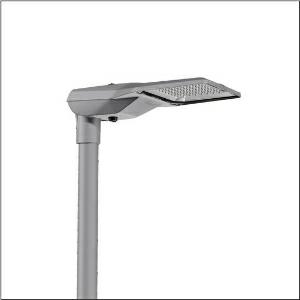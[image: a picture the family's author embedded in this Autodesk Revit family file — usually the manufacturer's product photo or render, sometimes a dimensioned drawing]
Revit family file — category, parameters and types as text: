
# Revit family: streetlight_sl_21_midi___pl52_5xe3h33t08mb_7712
name_source: partatom
category: Lighting Fixtures
units: mm (PartAtom-declared; Revit-internal decimal feet)

## family parameters
Cut with Voids When Loaded = No
Host = Face
Light Source = No
Part Type = Normal
Room Calculation Point = No
Round Connector Dimension = Use Diameter
Shared = No

## types (1)
- --- (1 x LED, 17960 lm, 136 W, 3000K)
    Apparent Load = 136 VA
    CIE Flux Codes = 27 59 98 100 100
    Color Rendering = 70
    Color Temperature = 3000K
    Default Elevation = 1800 mm
    Description = Streetlight SL 21 midi, mast luminaire, primary light control with lens, of PMMA, primary optical cover: cover, of toughened safety glass, transparent, light distribution: PL52, light emission: direct distribution, primary light characteristic: asymmetric, installation type: side-entry, post-top, LED, High Power LED, rated luminous flux: 17.960lm, luminous efficacy: 132lm/W, light colour: 730, colour temperature: 3000K, control gear: D4i, control: overheat protection, constant luminous flux control, time-dependent luminous flux control, flexible luminous flux parameterisation, pre-setting: logarithmic dimming characteristic, mains connection: 230..240V, AC, 50/60Hz, start of lifetime: 136W, end of service life: 142W, reduction: 61W, luminaire housing, of diecast aluminium, powder-coated, SITECO metallic grey (DB 702S), corrosivity category C5 high according to DIN EN ISO 12944, please order mast flange separately, inclination adjustable: 0°, 5°, 10°, 15°, sealing non-destructively replaceable, multi-level sealing system, length: 644mm, width: 335mm, height: 110mm, mast flange for spigot size: 42mm (side-entry): 5XC10008XM4, 60/48mm (side-entry/post-top): 5XC10108XM2, 76/60mm (side-entry/post-top): 5XC10108XM1, mounting height: 4..8m, Smart Interface below and above, protection rating (complete): IP66, insulation class (complete): insulation class II (safety insulation), certification: CE, ENEC, ENEC+, VDE, impact resistance: IK10, permissible operating ambient temperature for outdoor applications: -40..+50°C, standard-compliant lighting for roads and squares, packaging unit: 1 piece

Light Distribution: PL52
    Height = 111 mm
    Lamp = 1 x LED
    Lamp Light Flux = 17960 lm
    Lamp Power = 136 W
    Lamp count = 1
    Length = 644 mm
    Luminous efficacy = 132 lm/W
    Manufacturer = Siteco
    ModVariant = No
    Model = 5XE3H33T08MB
    Number of Poles = 1
    OnlyDefault = Yes
    Power Factor = 1
    Product Name = Streetlight SL 21 midi | PL52
    Product group = mast luminaire | pylon top
    ProductGroupID = 6100
    Protection Class = Protection class II
    Protection Degree = IP 66
    RLX_Detail_Level = 1
    RLX_Emergency_Light_Flux = 0 lm
    RLX_Emergency_Type = 0
    RLX_Emergency_Type_DB = No
    RlxData = <blob elided: 36653 chars, md5=68a0ea8b>
    Socket = socket
    Standby Power = 0 W
    System Light Flux = 17960 lm
    System Power = 136 W
    Type Comments = factory setting: luminous flux: 100 % | dim-lin: 254 | 695 mA
    Type Image = l_1004304.jpg
    URL = http://relux.com
    VarID = @adj_188053
    Voltage = 0 V
    Weight = 0.00 kg
    Width = 336 mm

## geometry (parser evidence)
native form markers: Blend x4, Sweep x8
no freeform markers — native parametric forms only
